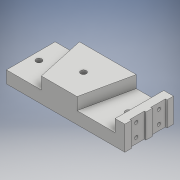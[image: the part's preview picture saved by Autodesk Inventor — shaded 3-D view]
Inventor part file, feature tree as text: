
AUTODESK INVENTOR PART (.ipt)
format: ipt  version: 2018 (Build 220112000, 112)  size: 208,896 bytes
history: native  units: mm
features: extrude x8, sketch x8, projected_geometry x2
ambient origin geometry x8: Origin, YZ Plane, XZ Plane, XY Plane, X Axis, Y Axis, Z Axis, Center Point
bodies: Solid1 (feature_tree)
feature tree (18):
  extrude  "Extrusion1"  Depth=30.0mm
  extrude  "Extrusion2"  Depth=22.0mm
  extrude  "Extrusion3"  Depth=15.0mm
  extrude  "Extrusion4"  Depth=7.5mm TaperAngle=0.0deg
  extrude  "Extrusion5"  Depth=5.0mm
  extrude  "Extrusion6"  Depth=7.5mm TaperAngle=0.0deg
  extrude  "Extrusion7"  Depth=6.0mm
  extrude  "Extrusion8"  Depth=3.0mm TaperAngle=0.0deg
  sketch  "Sketch1"  dims[d0=65.0mm d1=30.0mm]
  sketch  "Sketch2"  dims[d2=7.5mm d3=0.0mm d4=22.0mm]
  sketch  "Sketch3"  dims[d5=35.0mm d6=15.0mm]
  sketch  "Sketch4"  dims[d7=21.5mm d8=7.5mm d9=0.0mm]
  sketch  "Sketch5"  dims[d10=5.0mm d11=5.0mm]
  projected_geometry  "Projected Loop1"
  sketch  "Sketch6"  dims[d12=3.5mm d13=7.5mm d14=0.0mm]
  sketch  "Sketch7"  dims[d15=6.0mm d16=6.0mm]
  projected_geometry  "Projected Loop2"
  sketch  "Sketch8"  dims[d17=6.0mm d18=3.0mm d19=0.0mm d20=2.0mm d21=0.0mm d22=5.0mm d23=0.0mm d26=2.0mm d27=14.0mm d28=8.0mm d29=8.0mm d30=3.5mm d31=5.0mm d32=0.0mm d33=4.0mm d34=4.0mm d35=4.0mm d36=2.0mm d37=1.0mm d38=0.0mm]
